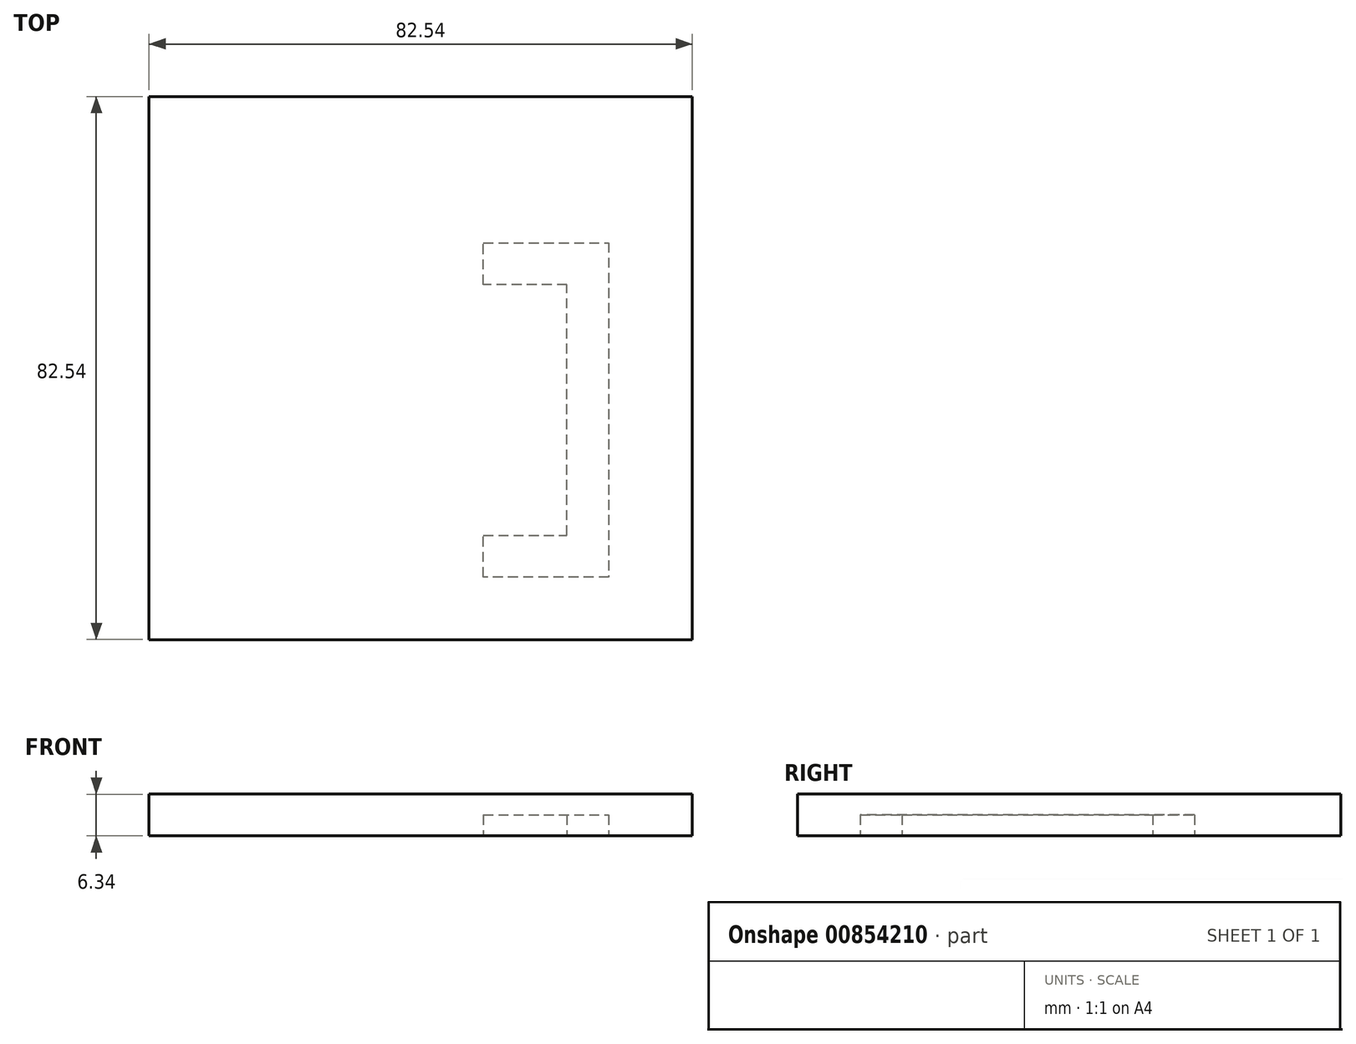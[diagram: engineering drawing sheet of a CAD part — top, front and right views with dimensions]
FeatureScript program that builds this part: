
annotation { "Feature Type Name" : "Feature", "Feature Type Description" : "" }
export const myFeature = defineFeature(function(context is Context, id is Id, definition is map)
    precondition{}
    {
        {
            var Q0;
            Q0=qCreatedBy(makeId("Top.planeOp"),FACE);
            var sketch = newSketch(context, id + "F0", { "sketchPlane" : qUnion([Q0])});
            skLineSegment(sketch, "E0.bottom", {"start": v(-41.27, 41.28) * mm, "end": v(41.28, 41.28) * mm});
            skLineSegment(sketch, "E0.top", {"start": v(-41.28, -41.28) * mm, "end": v(41.27, -41.28) * mm});
            skLineSegment(sketch, "E0.left", {"start": v(-41.27, 41.28) * mm, "end": v(-41.28, -41.27) * mm});
            skLineSegment(sketch, "E0.right", {"start": v(41.28, 41.28) * mm, "end": v(41.27, -41.27) * mm});
            skPoint(sketch, "E0.middle", {"position": v(0, 0) * mm});
            skSolve(sketch);
        }
        {
            var Q0;
            Q0=makeQuery(id+"F0.imprint","IMPRINT",FACE,{"disambiguationData":[TD([[makeQuery(id+"F0.imprint","IMPRINT",EDGE,{"derivedFrom":sQuery(id+"F0.wireOp",EDGE,"E0.bottom")}),-1.0]])]});
            extrude(context, id + "F1", {"entities" : qUnion([Q0]), "endBound" : BoundingType.SYMMETRIC, "depth" : 6.35 * mm, "offsetDistance" : 25.4 * mm});
        }
        {
            var Q0;
            Q0=makeQuery(id+"F1.opExtrude","CAP_FACE",FACE,{"disambiguationData":[OSD([sQuery(id+"F0.wireOp",EDGE,"E0.bottom"),sQuery(id+"F0.wireOp",EDGE,"E0.top"),sQuery(id+"F0.wireOp",EDGE,"E0.left"),sQuery(id+"F0.wireOp",EDGE,"E0.right")])],"isStart":true});
            var sketch = newSketch(context, id + "F2", { "sketchPlane" : qUnion([Q0])});
            skLineSegment(sketch, "E1", {"start": v(28.57, -19.05) * mm, "end": v(28.57, 31.75) * mm});
            skLineSegment(sketch, "E2", {"start": v(28.57, 31.75) * mm, "end": v(9.52, 31.75) * mm});
            skLineSegment(sketch, "E3", {"start": v(9.52, 31.75) * mm, "end": v(9.52, 25.4) * mm});
            skLineSegment(sketch, "E4", {"start": v(9.52, 25.4) * mm, "end": v(22.22, 25.4) * mm});
            skLineSegment(sketch, "E5", {"start": v(22.22, 25.4) * mm, "end": v(22.22, -12.7) * mm});
            skLineSegment(sketch, "E6", {"start": v(22.22, -12.7) * mm, "end": v(9.52, -12.7) * mm});
            skLineSegment(sketch, "E7", {"start": v(9.52, -12.7) * mm, "end": v(9.52, -19.05) * mm});
            skLineSegment(sketch, "E8", {"start": v(9.52, -19.05) * mm, "end": v(28.57, -19.05) * mm});
            skLineSegment(sketch, "E9", {"start": v(28.57, 0) * mm, "end": v(22.22, 0) * mm, "construction": true});
            skSolve(sketch);
        }
        {
            var Q0;
            Q0=makeQuery(id+"F2.imprint","IMPRINT",FACE,{"disambiguationData":[TD([[makeQuery(id+"F2.imprint","IMPRINT",EDGE,{"derivedFrom":sQuery(id+"F2.wireOp",EDGE,"E1")}),1.0]])]});
            extrude(context, id + "F3", {"entities" : qUnion([Q0]), "operationType" : NewBodyOperationType.REMOVE, "oppositeDirection" : true, "depth" : 3.17 * mm, "offsetDistance" : 25.4 * mm});
        }
    });
